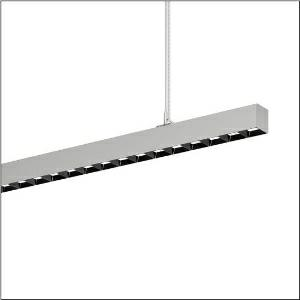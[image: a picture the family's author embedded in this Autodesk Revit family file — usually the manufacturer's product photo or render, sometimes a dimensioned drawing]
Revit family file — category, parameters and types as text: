
# Revit family: silica_r__21_51mx31tctds_9889
name_source: partatom
category: Lighting Fixtures
units: mm (PartAtom-declared; Revit-internal decimal feet)

## family parameters
Cut with Voids When Loaded = No
Host = Face
Light Source = No
Part Type = Normal
Room Calculation Point = No
Round Connector Dimension = Use Diameter
Shared = No

## types (1)
- --- (1 x LED, 15550 lm, 133.9 W, 6500K)
    Apparent Load = 134 VA
    CIE Flux Codes = 85 99 100 60 100
    Color Rendering = 80
    Color Temperature = 6500K
    Default Elevation = 1800 mm
    Description = Silica® 21, office luminaire, primary light control with darklight reflector, of PMMA, black, CAT 2 (L<= 3000cd/m²), light emission: direct/indirect distribution, primary light characteristic: symmetric, installation type: suspended mounting, LED, rated luminous flux: 15.550lm, luminous efficacy: 111lm/W, light colour: 8tw, colour temperature: 2700..6500K, control gear: DALI DT8, with terminal, 3+2-pole, max. 2.5mm², mains connection: 220..240V, AC, 50/60Hz, rated input power: 140.6W, luminaire housing, of aluminium, metallic grey (RAL 9006), length: 3.004mm, width: 53mm, height: 53mm, protection rating (complete): IP20, insulation class (complete): insulation class I (protective earthing), certification: CE, permissible operating ambient temperature: 0..+35°C, standard: EN 50419, packaging unit: 1 piece
    Height = 53 mm
    Lamp = 1 x LED
    Lamp Light Flux = 15550 lm
    Lamp Power = 133.9 W
    Lamp count = 1
    Length = 3004 mm
    Luminous efficacy = 116 lm/W
    Manufacturer = Siteco
    ModVariant = No
    Model = 51MX31TCTDS
    Mounting Place = Ceiling
    Mounting Type = Pendant
    Number of Poles = 1
    OnlyDefault = Yes
    Power Factor = 1
    Product Name = Silica® 21
    Product group = office luminaire | ceiling pendant
    ProductGroupID = 904
    Protection Class = Protection class I
    Protection Degree = IP 20
    RLX_Detail_Level = 1
    RLX_Emergency_Light_Flux = 0 lm
    RLX_Emergency_Type = 0
    RLX_Emergency_Type_DB = No
    RlxData = <blob elided: 61697 chars, md5=56b7c623>
    Socket = socket
    Standby Power = 0 W
    System Light Flux = 15550 lm
    System Power = 134 W
    Type Comments = individual setting
    Type Image = l_1335859.jpg
    URL = http://relux.com
    VarID = @adj_139860
    Voltage = 0 V
    Weight = 0.00 kg
    Width = 53 mm

## geometry (parser evidence)
native form markers: Blend x4, Sweep x12
no freeform markers — native parametric forms only
